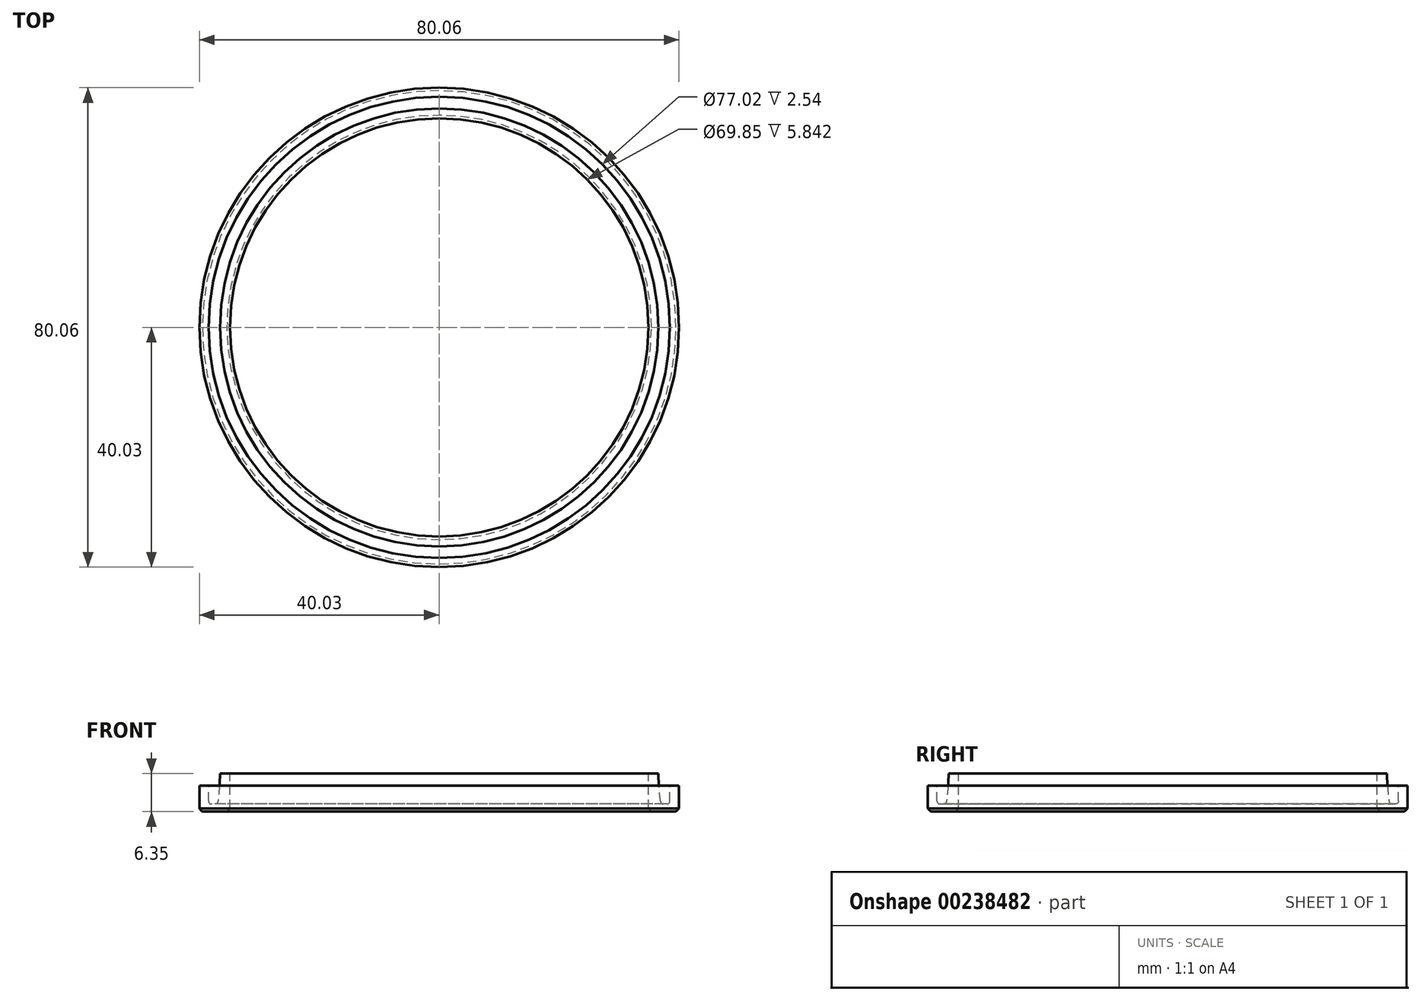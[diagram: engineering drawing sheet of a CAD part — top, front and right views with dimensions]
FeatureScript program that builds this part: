
annotation { "Feature Type Name" : "Feature", "Feature Type Description" : "" }
export const myFeature = defineFeature(function(context is Context, id is Id, definition is map)
    precondition{}
    {
        {
            var Q0;
            Q0=qCreatedBy(makeId("Front.planeOp"),FACE);
            var sketch = newSketch(context, id + "F0", { "sketchPlane" : qUnion([Q0])});
            skLineSegment(sketch, "E0", {"start": v(-40.03, 4.32) * mm, "end": v(-40.03, 0) * mm});
            skLineSegment(sketch, "E1", {"start": v(-40.03, 0) * mm, "end": v(-34.93, 0) * mm});
            skLineSegment(sketch, "E2", {"start": v(-34.93, 0) * mm, "end": v(-34.93, 6.35) * mm});
            skLineSegment(sketch, "E3", {"start": v(-37.44, 1.27) * mm, "end": v(-38, 1.27) * mm});
            skLineSegment(sketch, "E4", {"start": v(-38.5, 1.78) * mm, "end": v(-38.5, 4.32) * mm});
            skLineSegment(sketch, "E5", {"start": v(-38.5, 4.32) * mm, "end": v(-40.03, 4.32) * mm});
            skLineSegment(sketch, "E6", {"start": v(-34.93, 6.35) * mm, "end": v(-36.58, 6.35) * mm});
            skFitSpline(sketch, "E7", {"points": [v(-36.98, 1.27) * mm, v(-36.68, 4.12) * mm, v(-36.58, 6.35) * mm], "startDerivative": vector(0.6, 5.23) * mm, "endDerivative": vector(0.07, 2.6) * mm});
            skLineSegment(sketch, "E8", {"start": v(-37.75, 0.8) * mm, "end": v(-37.75, 4.2) * mm, "construction": true});
            skPoint(sketch, "E8.startSnap0", {"position": v(-37.75, 1.27) * mm});
            skPoint(sketch, "E9.visualSharp", {"position": v(-38.5, 1.27) * mm});
            skArc(sketch, "E9.filletArc", {"start": v(-38.5, 1.78) * mm, "mid": v(-38.36, 1.42) * mm, "end": v(-38, 1.27) * mm});
            skArc(sketch, "E10.filletArc", {"start": v(-37.44, 1.27) * mm, "mid": v(-37.1, 1.4) * mm, "end": v(-36.93, 1.72) * mm});
            skLineSegment(sketch, "E11", {"start": v(0, 45.51) * mm, "end": v(0, -21.7) * mm, "construction": true});
            skSolve(sketch);
        }
        {
            var Q0;
            Q0 = qSketchRegion(id + "F0", true);
            var Q1;
            Q1=sQuery(id+"F0.wireOp",EDGE,"E11");
            revolve(context, id + "F1", {"entities" : qUnion([Q0]), "axis" : qUnion([Q1]), "revolveType" : RevolveType.FULL});
        }
        {
            var Q0;
            Q0=makeQuery(id+"F1.opRevolve","SWEPT_FACE",FACE,{"disambiguationData":[OSD([sQuery(id+"F0.wireOp",EDGE,"E1")])]});
            chamfer(context, id + "F2", {"entities" : qUnion([Q0]), "width" : 0.5 * mm, "tangentPropagation" : true});
        }
    });
